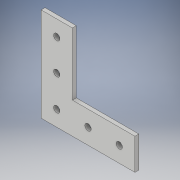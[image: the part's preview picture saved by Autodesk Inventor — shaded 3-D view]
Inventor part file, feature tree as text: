
AUTODESK INVENTOR PART (.ipt)
format: ipt  version: 2018 (Build 220112000, 112)  size: 111,104 bytes
history: native  units: in
note: dims shown in document units (in); Inventor stores cm internally (conversion verified against a paired STEP export)
features: extrude x1, sketch x1
ambient origin geometry x8: Origin, YZ Plane, XZ Plane, XY Plane, X Axis, Y Axis, Z Axis, Center Point
bodies: Solid1 (feature_tree)
feature tree (2):
  extrude  "Extrusion1"  Depth=1.0in
  sketch  "Sketch1"  dims[d0=3.0in d1=1.0in d2=1.0in d3=3.0in d4=0.5in d5=1.0in d6=1.0in d7=1.0in d8=1.0in d9=0.2031in d10=0.125in d11=0.0in]
